# Revit family: Toilet_Elongated-American_Standard-Champion_Pro-3195A101_Series
name_source: partatom
category: Plumbing Fixtures
units: mm (PartAtom-declared; Revit-internal decimal feet)

## family parameters
Always vertical = No
Cut with Voids When Loaded = No
OmniClass Number = 23.45.05.21.11.11
OmniClass Title = Water Operated Water Closets
Part Type = Normal
Room Calculation Point = No
Round Connector Dimension = Use Radius
Shared = Yes
Work Plane-Based = Yes

## types (3) — shared parameters
4225A.004 Tank = No
4225A.005 Tank complete with trip lever located = No
4225A.064 Tank complete with tank cover = No
ADA Compliant = Yes
Assembly Code = D2010110
Bowl Shape = Elongated
CEC Compliant = Yes
CW Connection = Yes
CWFU = 10
Cold Water Connection Diameter = 1/2"
Cold Water Connection Height = 10"
Cold Water Connection Radius = 1/4"
Cold Water Connection Width = 6"
Compliance Certifications = Meets or Exceeds• ASME A112.19.2-2008/CSA B45.1-08 for Vitreous China Fixtures• US EPA WaterSense Specification for HETs
Default Elevation = 0"
Description = Champion® PRO Chair Height Elongated Bowl
Flush Rate = (1.6 gpf/6.0 Lpf)
HW Connection = No
Height = 16 1/2"
Installation Type = Floor Mounted
Manufacturer = American Standard
Product Documentation Link = https://americanstandard.box.com
Product Page URL = https://www.americanstandard-us.com
Seat 5325.010 Elongated Champion Slow Close = No
URL = http://www.americanstandard-us.com
Vent Connection = No
WFU = 10
Warranty Information = 10 year warranty
Waste Connection = Yes
Waste Connection Diameter = 2 3/8"
Waste Connection Radius = 1 3/16"
Waste Connection Rough In = 12"
Width = 14"
zero-valued in all types: HWFU

## per-type parameters (varying)
| type | Finish | Material |
| 3195A101.020 | Vitreous China-American Standard-020-White | Vitreous China-American Standard-020-White |
| 3195A101.021 | Vitreous China-American Standard-021-Bone | Vitreous China-American Standard-021-Bone |
| 3195A101.222 | Vitreous China-American Standard-222-Linen | Vitreous China-American Standard-222-Linen |

note: column(s) folded — value = type name in every type: Model

## geometry (parser evidence)
native form markers: Sweep x2
no freeform markers — native parametric forms only
